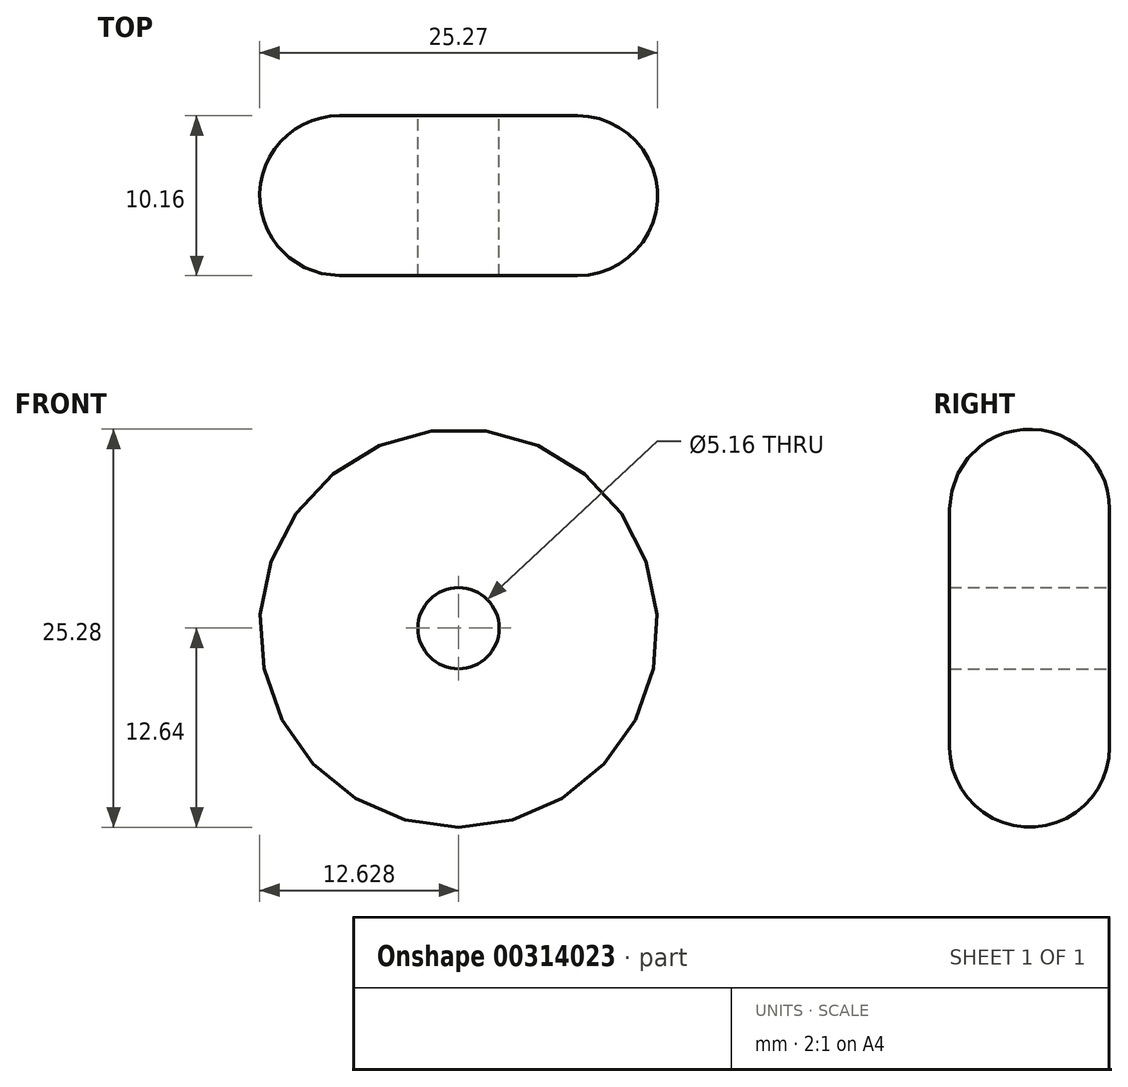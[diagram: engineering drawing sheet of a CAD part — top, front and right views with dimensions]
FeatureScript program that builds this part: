
annotation { "Feature Type Name" : "Feature", "Feature Type Description" : "" }
export const myFeature = defineFeature(function(context is Context, id is Id, definition is map)
    precondition{}
    {
        {
            var Q0;
            Q0=qCreatedBy(makeId("Front.planeOp"),FACE);
            var sketch = newSketch(context, id + "F0", { "sketchPlane" : qUnion([Q0])});
            skCircle(sketch, "E0", {"center": v(-57.7, 0) * mm, "radius": 12.64 * mm});
            skSolve(sketch);
        }
        {
            var Q0;
            Q0 = qSketchRegion(id + "F0", true);
            extrude(context, id + "F1", {"entities" : qUnion([Q0]), "depth" : 10.16 * mm});
        }
        {
            var Q0;
            Q0=makeQuery(id+"F1.opExtrude","CAP_FACE",FACE,{"disambiguationData":[OSD([sQuery(id+"F0.wireOp",EDGE,"E0")])],"isStart":true});
            var Q1;
            Q1=makeQuery(id+"F1.opExtrude","CAP_FACE",FACE,{"disambiguationData":[OSD([sQuery(id+"F0.wireOp",EDGE,"E0")])],"isStart":false});
            fillet(context, id + "F2", {"entities" : qUnion([Q0, Q1]), "radius" : 5.08 * mm, "tangentPropagation" : true, "allowEdgeOverflow" : false});
        }
        {
            var Q0;
            Q0=qCreatedBy(makeId("Front.planeOp"),FACE);
            var sketch = newSketch(context, id + "F3", { "sketchPlane" : qUnion([Q0])});
            skCircle(sketch, "E1", {"center": v(-57.71, 0) * mm, "radius": 2.58 * mm});
            skSolve(sketch);
        }
        {
            var Q0;
            Q0 = qSketchRegion(id + "F3", true);
            extrude(context, id + "F4", {"entities" : qUnion([Q0]), "operationType" : NewBodyOperationType.REMOVE, "depth" : 25.4 * mm});
        }
    });
